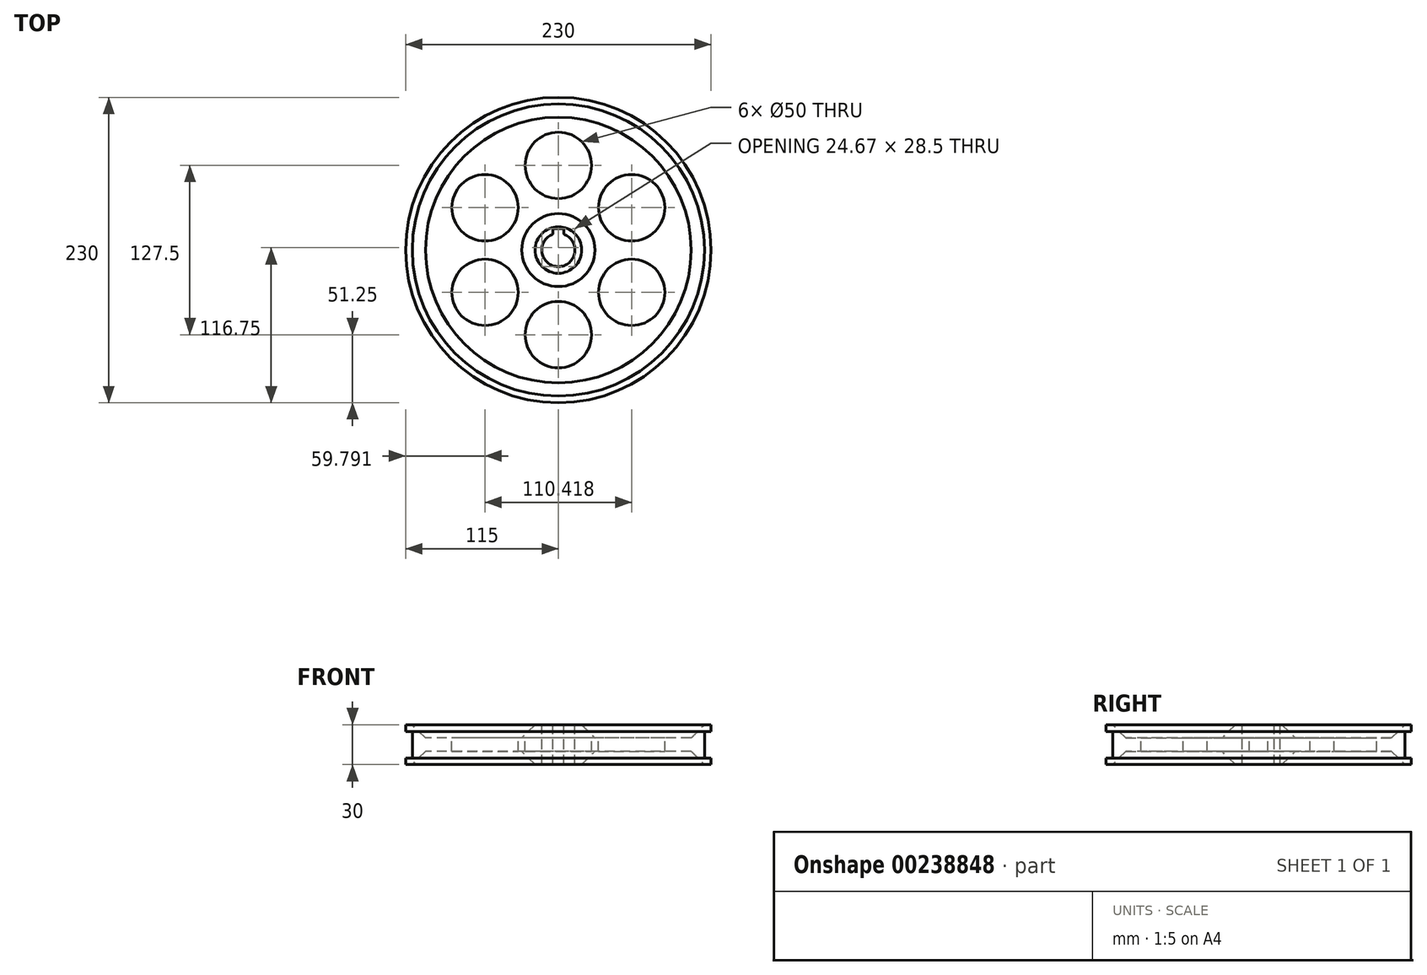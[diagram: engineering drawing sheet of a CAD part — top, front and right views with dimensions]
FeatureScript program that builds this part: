
annotation { "Feature Type Name" : "Feature", "Feature Type Description" : "" }
export const myFeature = defineFeature(function(context is Context, id is Id, definition is map)
    precondition{}
    {
        {
            var Q0;
            Q0=qCreatedBy(makeId("Front.planeOp"),FACE);
            var sketch = newSketch(context, id + "F0", { "sketchPlane" : qUnion([Q0])});
            skLineSegment(sketch, "E0", {"start": v(0, 62.7) * mm, "end": v(0, -67.54) * mm, "construction": true});
            skLineSegment(sketch, "E1", {"start": v(12.5, 15) * mm, "end": v(12.5, -15) * mm});
            skLineSegment(sketch, "E2", {"start": v(12.5, 15) * mm, "end": v(17.5, 15) * mm});
            skLineSegment(sketch, "E3", {"start": v(17.5, 15) * mm, "end": v(27.5, 5) * mm});
            skLineSegment(sketch, "E4", {"start": v(27.5, 5) * mm, "end": v(100, 5) * mm});
            skLineSegment(sketch, "E5", {"start": v(100, 5) * mm, "end": v(110, 15) * mm});
            skLineSegment(sketch, "E6", {"start": v(110, 15) * mm, "end": v(115, 15) * mm});
            skLineSegment(sketch, "E7", {"start": v(115, 15) * mm, "end": v(115, 10) * mm});
            skLineSegment(sketch, "E8", {"start": v(115, -10) * mm, "end": v(115, -15) * mm});
            skLineSegment(sketch, "E9", {"start": v(115, -15) * mm, "end": v(110, -15) * mm});
            skLineSegment(sketch, "E10", {"start": v(110, -15) * mm, "end": v(100, -5) * mm});
            skLineSegment(sketch, "E11", {"start": v(100, -5) * mm, "end": v(27.5, -5) * mm});
            skLineSegment(sketch, "E12", {"start": v(27.5, -5) * mm, "end": v(17.5, -15) * mm});
            skLineSegment(sketch, "E13", {"start": v(17.5, -15) * mm, "end": v(12.5, -15) * mm});
            skLineSegment(sketch, "E14", {"start": v(115, 10) * mm, "end": v(110, 10) * mm});
            skLineSegment(sketch, "E15", {"start": v(110, 10) * mm, "end": v(110, -10) * mm});
            skLineSegment(sketch, "E16", {"start": v(110, -10) * mm, "end": v(115, -10) * mm});
            skSolve(sketch);
        }
        {
            var Q0;
            Q0=makeQuery(id+"F0.imprint","IMPRINT",FACE,{"disambiguationData":[TD([[makeQuery(id+"F0.imprint","IMPRINT",EDGE,{"derivedFrom":sQuery(id+"F0.wireOp",EDGE,"E1")}),1.0]])]});
            var Q1;
            Q1=sQuery(id+"F0.wireOp",EDGE,"E0");
            revolve(context, id + "F1", {"entities" : qUnion([Q0]), "axis" : qUnion([Q1]), "revolveType" : RevolveType.FULL});
        }
        {
            var Q0;
            Q0=makeQuery(id+"F1.opRevolve","SWEPT_FACE",FACE,{"disambiguationData":[OSD([sQuery(id+"F0.wireOp",EDGE,"E2")])]});
            var sketch = newSketch(context, id + "F2", { "sketchPlane" : qUnion([Q0])});
            skCircle(sketch, "E17", {"center": v(0, 63.75) * mm, "radius": 25 * mm});
            skCircle(sketch, "E18.1.0", {"center": v(-55.2, 31.87) * mm, "radius": 25 * mm});
            skCircle(sketch, "E18.2.0", {"center": v(-55.2, -31.87) * mm, "radius": 25 * mm});
            skCircle(sketch, "E18.3.0", {"center": v(0, -63.75) * mm, "radius": 25 * mm});
            skCircle(sketch, "E18.4.0", {"center": v(55.2, -31.88) * mm, "radius": 25 * mm});
            skCircle(sketch, "E18.5.0", {"center": v(55.2, 31.87) * mm, "radius": 25 * mm});
            skPoint(sketch, "E18.center", {"position": v(0, 0) * mm});
            skLineSegment(sketch, "E19.bottom", {"start": v(-4, 0) * mm, "end": v(4, 0) * mm});
            skLineSegment(sketch, "E19.top", {"start": v(-4, 16) * mm, "end": v(4, 16) * mm});
            skLineSegment(sketch, "E19.left", {"start": v(-4, 0) * mm, "end": v(-4, 16) * mm});
            skLineSegment(sketch, "E19.right", {"start": v(4, 0) * mm, "end": v(4, 16) * mm});
            skSolve(sketch);
        }
        {
            var Q0;
            Q0=makeQuery(id+"F2.imprint","IMPRINT",FACE,{"disambiguationData":[TD([[makeQuery(id+"F2.imprint","IMPRINT",EDGE,{"derivedFrom":sQuery(id+"F2.wireOp",EDGE,"E18.1.0")}),1.0]])]});
            var Q1;
            Q1=makeQuery(id+"F2.imprint","IMPRINT",FACE,{"disambiguationData":[TD([[makeQuery(id+"F2.imprint","IMPRINT",EDGE,{"derivedFrom":sQuery(id+"F2.wireOp",EDGE,"E17")}),1.0]])]});
            var Q2;
            Q2=makeQuery(id+"F2.imprint","IMPRINT",FACE,{"disambiguationData":[TD([[makeQuery(id+"F2.imprint","IMPRINT",EDGE,{"derivedFrom":sQuery(id+"F2.wireOp",EDGE,"E18.5.0")}),1.0]])]});
            var Q3;
            Q3=makeQuery(id+"F2.imprint","IMPRINT",FACE,{"disambiguationData":[TD([[makeQuery(id+"F2.imprint","IMPRINT",EDGE,{"derivedFrom":sQuery(id+"F2.wireOp",EDGE,"E18.4.0")}),1.0]])]});
            var Q4;
            Q4=makeQuery(id+"F2.imprint","IMPRINT",FACE,{"disambiguationData":[TD([[makeQuery(id+"F2.imprint","IMPRINT",EDGE,{"derivedFrom":sQuery(id+"F2.wireOp",EDGE,"E18.3.0")}),1.0]])]});
            var Q5;
            Q5=makeQuery(id+"F2.imprint","IMPRINT",FACE,{"disambiguationData":[TD([[makeQuery(id+"F2.imprint","IMPRINT",EDGE,{"derivedFrom":sQuery(id+"F2.wireOp",EDGE,"E18.2.0")}),1.0]])]});
            var Q6;
            {var subQ0=sQuery(id+"F2.wireOp",EDGE,"E19.top");Q6=makeQuery(id+"F2.imprint","IMPRINT",FACE,{"disambiguationData":[TD([[makeQuery(id+"F2.imprint","IMPRINT",EDGE,{"derivedFrom":subQ0}),-1.0]])]});}
            extrude(context, id + "F3", {"entities" : qUnion([Q0, Q1, Q2, Q3, Q4, Q5, Q6]), "operationType" : NewBodyOperationType.REMOVE, "endBound" : BoundingType.THROUGH_ALL, "oppositeDirection" : true, "depth" : 25 * mm});
        }
    });
